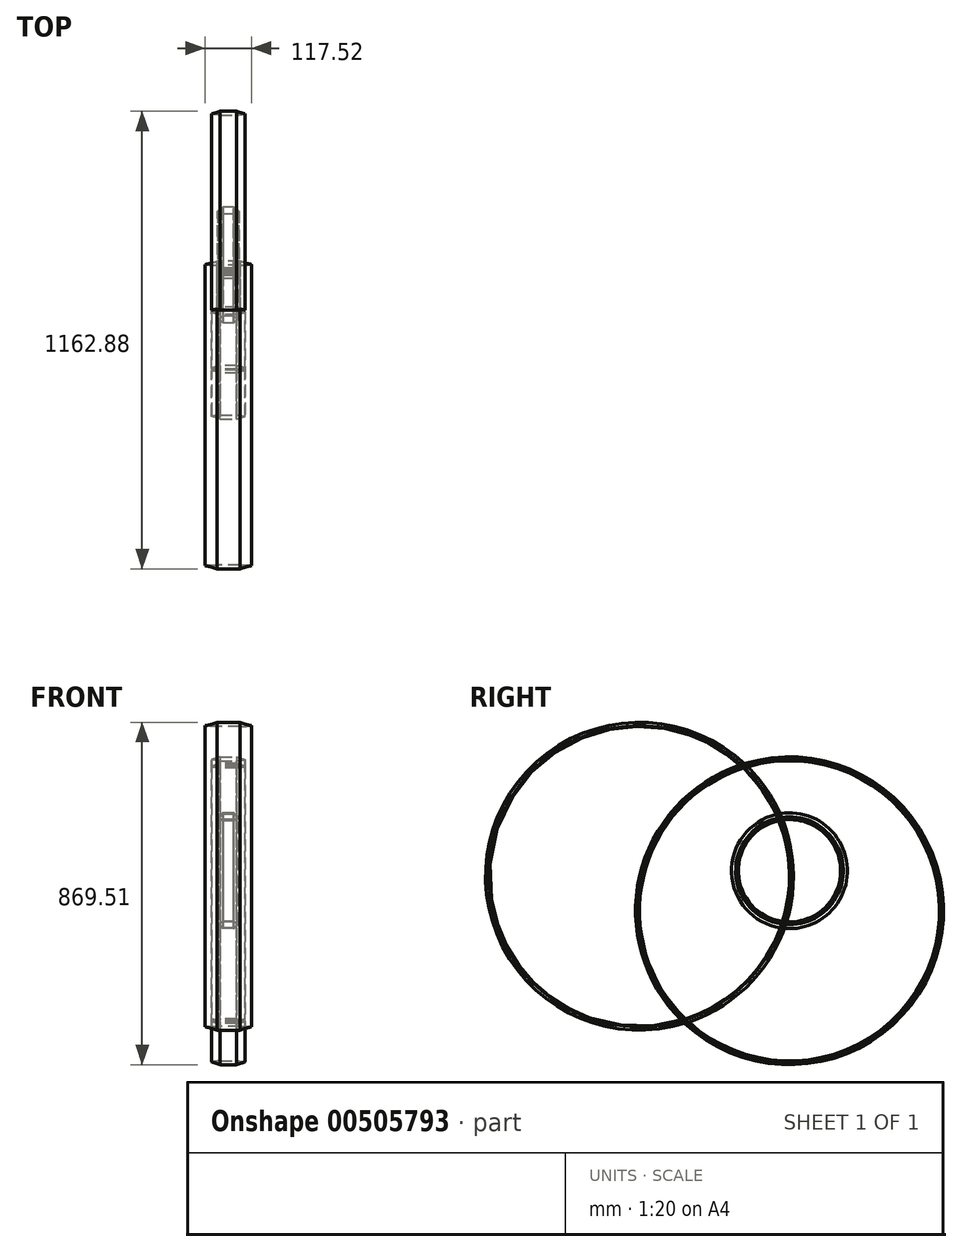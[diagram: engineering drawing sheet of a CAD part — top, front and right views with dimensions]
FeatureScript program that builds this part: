
annotation { "Feature Type Name" : "Feature", "Feature Type Description" : "" }
export const myFeature = defineFeature(function(context is Context, id is Id, definition is map)
    precondition{}
    {
        {
            var Q0;
            Q0=qCreatedBy(makeId("Front.planeOp"),FACE);
            var sketch = newSketch(context, id + "F0", { "sketchPlane" : qUnion([Q0])});
            skCircle(sketch, "E0.cCircle", {"center": v(0, 0) * mm, "radius": 58.76 * mm, "construction": true});
            skLineSegment(sketch, "E0.0", {"start": v(58.76, 0) * mm, "end": v(29.38, -50.89) * mm});
            skLineSegment(sketch, "E0.1", {"start": v(29.38, -50.89) * mm, "end": v(-29.38, -50.89) * mm});
            skLineSegment(sketch, "E0.2", {"start": v(-29.38, -50.89) * mm, "end": v(-58.76, 0) * mm});
            skLineSegment(sketch, "E0.3", {"start": v(-58.76, 0) * mm, "end": v(-29.38, 50.89) * mm});
            skLineSegment(sketch, "E0.4", {"start": v(-29.38, 50.89) * mm, "end": v(29.38, 50.89) * mm});
            skLineSegment(sketch, "E0.5", {"start": v(29.38, 50.89) * mm, "end": v(58.76, 0) * mm});
            skSolve(sketch);
        }
        {
            var Q0;
            Q0=qCreatedBy(makeId("Front.planeOp"),FACE);
            cPlane(context, id + "F1", {"entities" : qUnion([Q0]), "cplaneType" : CPlaneType.OFFSET, "offset" : 127 * mm, "width" : 152.4 * mm, "height" : 152.4 * mm});
        }
        {
            var Q0;
            Q0=qCreatedBy(id+"F1.planeOp",FACE);
            var sketch = newSketch(context, id + "F2", { "sketchPlane" : qUnion([Q0])});
            skCircle(sketch, "E1.cCircle", {"center": v(0, 0) * mm, "radius": 26.9 * mm, "construction": true});
            skLineSegment(sketch, "E1.0", {"start": v(26.9, 0) * mm, "end": v(13.45, -23.29) * mm});
            skLineSegment(sketch, "E1.1", {"start": v(13.45, -23.29) * mm, "end": v(-13.45, -23.29) * mm});
            skLineSegment(sketch, "E1.2", {"start": v(-13.45, -23.29) * mm, "end": v(-26.9, 0) * mm});
            skLineSegment(sketch, "E1.3", {"start": v(-26.9, 0) * mm, "end": v(-13.45, 23.29) * mm});
            skLineSegment(sketch, "E1.4", {"start": v(-13.45, 23.29) * mm, "end": v(13.45, 23.29) * mm});
            skLineSegment(sketch, "E1.5", {"start": v(13.45, 23.29) * mm, "end": v(26.9, 0) * mm});
            skSolve(sketch);
        }
        {
            var Q0;
            Q0=qCreatedBy(id+"F1.planeOp",FACE);
            cPlane(context, id + "F3", {"entities" : qUnion([Q0]), "cplaneType" : CPlaneType.OFFSET, "offset" : 254 * mm, "width" : 152.4 * mm, "height" : 152.4 * mm});
        }
        {
            var Q0;
            Q0=qCreatedBy(id+"F3.planeOp",FACE);
            var sketch = newSketch(context, id + "F4", { "sketchPlane" : qUnion([Q0])});
            skCircle(sketch, "E2.cCircle", {"center": v(0, 0) * mm, "radius": 42.41 * mm, "construction": true});
            skLineSegment(sketch, "E2.0", {"start": v(42.41, 0) * mm, "end": v(21.2, -36.73) * mm});
            skLineSegment(sketch, "E2.1", {"start": v(21.2, -36.73) * mm, "end": v(-21.2, -36.73) * mm});
            skLineSegment(sketch, "E2.2", {"start": v(-21.2, -36.73) * mm, "end": v(-42.41, 0) * mm});
            skLineSegment(sketch, "E2.3", {"start": v(-42.41, 0) * mm, "end": v(-21.2, 36.73) * mm});
            skLineSegment(sketch, "E2.4", {"start": v(-21.2, 36.73) * mm, "end": v(21.2, 36.73) * mm});
            skLineSegment(sketch, "E2.5", {"start": v(21.2, 36.73) * mm, "end": v(42.41, 0) * mm});
            skSolve(sketch);
        }
        {
            var Q0;
            Q0=makeQuery(id+"F4.imprint","IMPRINT",FACE,{"disambiguationData":[TD([[makeQuery(id+"F4.imprint","IMPRINT",EDGE,{"derivedFrom":sQuery(id+"F4.wireOp",EDGE,"E2.0")}),-1.0]])]});
            var Q1;
            Q1=sQuery(id+"F0.wireOp",EDGE,"E0.1");
            revolve(context, id + "F5", {"entities" : qUnion([Q0]), "axis" : qUnion([Q1]), "revolveType" : RevolveType.FULL});
        }
        {
            var Q0;
            Q0=makeQuery(id+"F2.imprint","IMPRINT",FACE,{"disambiguationData":[TD([[makeQuery(id+"F2.imprint","IMPRINT",EDGE,{"derivedFrom":sQuery(id+"F2.wireOp",EDGE,"E1.0")}),-1.0]])]});
            var Q1;
            Q1=sQuery(id+"F0.wireOp",EDGE,"E0.4");
            revolve(context, id + "F6", {"entities" : qUnion([Q0]), "axis" : qUnion([Q1]), "revolveType" : RevolveType.FULL});
        }
        {
            var Q0;
            Q0=makeQuery(id+"F0.imprint","IMPRINT",FACE,{"disambiguationData":[TD([[makeQuery(id+"F0.imprint","IMPRINT",EDGE,{"derivedFrom":sQuery(id+"F0.wireOp",EDGE,"E0.0")}),-1.0]])]});
            var Q1;
            Q1=sQuery(id+"F4.wireOp",EDGE,"E2.4");
            revolve(context, id + "F7", {"operationType" : NewBodyOperationType.ADD, "entities" : qUnion([Q0]), "axis" : qUnion([Q1]), "revolveType" : RevolveType.FULL});
        }
    });
